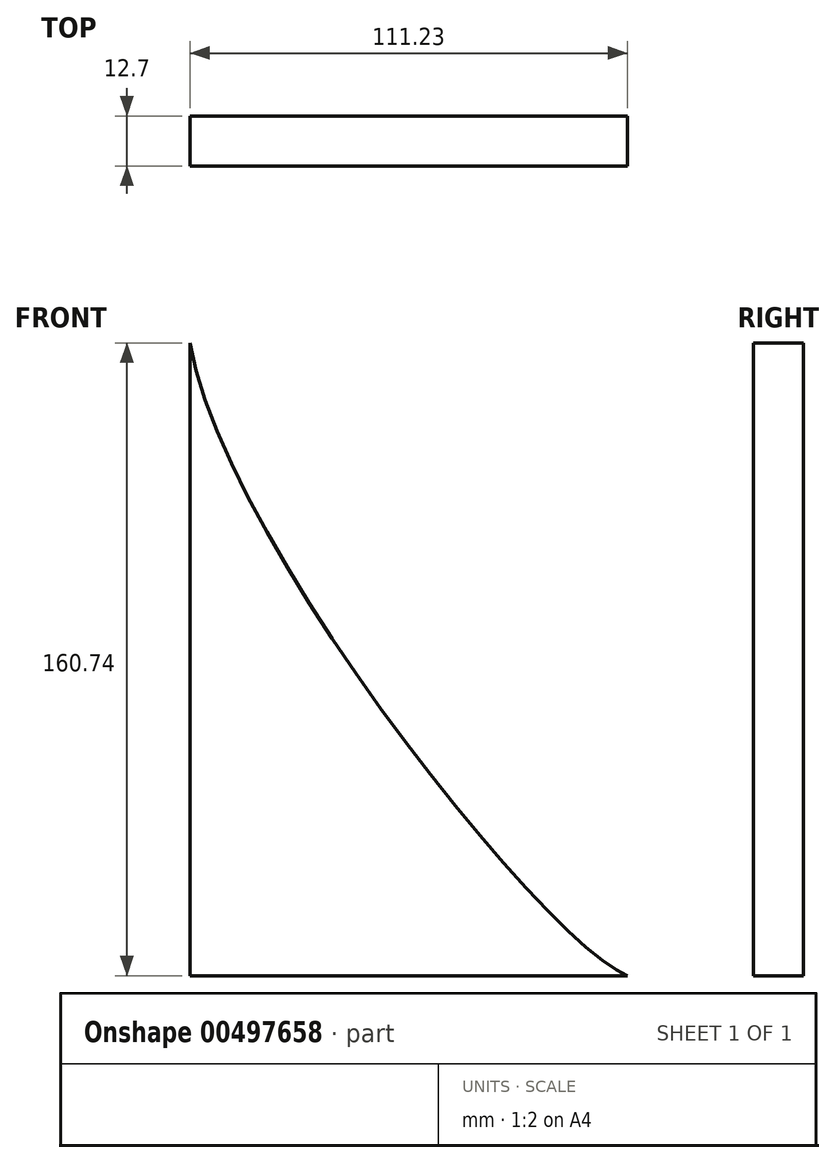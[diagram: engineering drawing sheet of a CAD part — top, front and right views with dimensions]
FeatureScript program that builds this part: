
annotation { "Feature Type Name" : "Feature", "Feature Type Description" : "" }
export const myFeature = defineFeature(function(context is Context, id is Id, definition is map)
    precondition{}
    {
        {
            var Q0;
            Q0=qCreatedBy(makeId("Front.planeOp"),FACE);
            var sketch = newSketch(context, id + "F0", { "sketchPlane" : qUnion([Q0])});
            skLineSegment(sketch, "E0.bottom", {"start": v(-39.89, 96.78) * mm, "end": v(-39.89, 96.78) * mm});
            skLineSegment(sketch, "E0.top", {"start": v(-62.5, -98.4) * mm, "end": v(48.74, -98.4) * mm});
            skLineSegment(sketch, "E0.left", {"start": v(-62.5, 79.4) * mm, "end": v(-62.5, -98.4) * mm});
            skFitSpline(sketch, "E1", {"points": [v(-62.5, 62.34) * mm, v(-39.89, 96.78) * mm, v(35.1, 18.57) * mm, v(54.86, -42.35) * mm, v(57.45, -65.65) * mm, v(55, -93.32) * mm, v(48.74, -98.4) * mm, v(-62.5, 62.34) * mm]});
            skCircle(sketch, "E2", {"center": v(-46.86, 64.79) * mm, "radius": 6.35 * mm});
            skCircle(sketch, "E3", {"center": v(-46.86, 42.25) * mm, "radius": 6.35 * mm});
            skSolve(sketch);
        }
        {
            var Q0;
            Q0=makeQuery(id+"F0.imprint","IMPRINT",FACE,{"disambiguationData":[TD([[makeQuery(id+"F0.imprint","IMPRINT",EDGE,{"derivedFrom":sQuery(id+"F0.wireOp",EDGE,"E0.top")}),1.0]])]});
            extrude(context, id + "F1", {"entities" : qUnion([Q0]), "depth" : 12.7 * mm});
        }
    });
